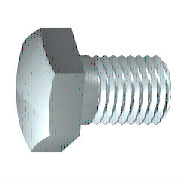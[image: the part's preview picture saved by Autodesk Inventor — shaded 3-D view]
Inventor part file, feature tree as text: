
AUTODESK INVENTOR PART (.ipt)
format: ipt  version: 2023.2 (Build 272271030, 271C)  size: 193,024 bytes
history: native  units: mm (DEFAULTED — no unit token found)
features: sketch x3, extrude x1, chamfer x1, plane x1
ambient origin geometry x7: Origin, YZ Plane, XZ Plane, X Axis, Y Axis, Z Axis, Center Point
bodies: Solid1 (feature_tree), Body (feature_tree)
feature tree (6):
  extrude  "Head"  Depth=35.5mm
  chamfer  "Chamfer1"  Distance=5.8mm
  plane  "Work Plane1"
  sketch  "Sketch1"  dims[d0=40.0mm d1=35.5mm]
  sketch  "Sketch2"  dims[d2=10.0mm]
  sketch  "Sketch4"  dims[d12=90.0deg d3=5.8mm d4=0.0mm d5=30.0deg d21=90.0deg d6=0.920175mm d7=0.920275mm d8=0.0mm d9=0.6001mm d10=14.63mm d11=16.0mm d13=0.920275mm d14=10.0mm d15=35.5mm d16=0.0mm d19=16.0mm d55=45.0deg d57=0.0mm d58=0.0mm]
